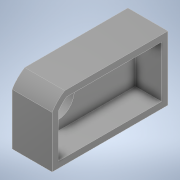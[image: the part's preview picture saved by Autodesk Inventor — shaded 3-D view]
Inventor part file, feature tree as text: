
AUTODESK INVENTOR PART (.ipt)
format: ipt  version: 2022 (Build 260153000, 153)  size: 385,024 bytes
history: mixed  units: in
note: dims shown in document units (in); Inventor stores cm internally (conversion verified against a paired STEP export)
features: extrude x5, sketch x5, other x2, plane x1, imported_body x1
ambient origin geometry x8: Origin, YZ Plane, XZ Plane, XY Plane, X Axis, Y Axis, Z Axis, Center Point
bodies: Solid1 (imported_parasolid)
feature tree (14):
  other  "Repaired Geometry1"
  plane  "Work Plane1"
  extrude  "Extrusion1"  Depth=0.0405in TaperAngle=0.0deg
  extrude  "Extrusion3"  Depth=0.9843in TaperAngle=0.0deg
  extrude  "Extrusion4"  Depth=0.3937in
  extrude  "Extrusion5"  [1 undecoded]
  extrude  "Extrusion6"  [1 undecoded]
  sketch  "Sketch2"  dims[d2=1.0236in d3=0.0787in d4=0.0in d5=0.0in d9=0.0405in d10=0.0in]
  other  "96_Teeth_Gear.STEP"
  sketch  "Sketch4"  dims[d11=0.2362in d12=0.9843in d13=0.0in]
  sketch  "Sketch5"  dims[d14=0.3937in d15=0.0in d16=1.2638in]
  sketch  "Sketch6"  dims[d17=0.5118in d18=0.0in]
  sketch  "Sketch7"
  imported_body  NMx_Import_Brep_tag  [imported B-rep: ~14 faces, bbox_mm=[38.0, 61.028, 110.0]]
note: 2 required parameter values undecoded (feature->parameter linkage not recoverable at this tier; creation-order binding heuristic only, values carry confidence <= 0.55)
